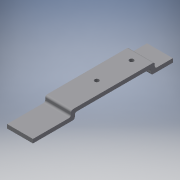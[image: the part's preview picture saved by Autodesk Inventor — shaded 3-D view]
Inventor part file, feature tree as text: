
AUTODESK INVENTOR PART (.ipt)
format: ipt  version: 2016 (Build 200138000, 138)  size: 158,208 bytes
history: native  units: mm
features: reference x9, extrude x5, sketch x5, fillet x1
ambient origin geometry x8: Origin, YZ Plane, XZ Plane, XY Plane, X Axis, Y Axis, Z Axis, Center Point
bodies: Solid1 (feature_tree)
feature tree (20):
  extrude  "Extrusion1"  Depth=130.0mm
  extrude  "Extrusion2"  Depth=6.0mm TaperAngle=0.0deg
  extrude  "Extrusion3"  Depth=6.0mm
  extrude  "Extrusion4"  Depth=34.0mm
  fillet  "Fillet1"  Radius=65.0mm
  extrude  "Extrusion5"  Depth=40.0mm
  sketch  "Sketch1"  dims[d0=40.0mm d1=130.0mm]
  sketch  "Sketch2"  dims[d2=6.0mm d3=0.0mm d4=6.0mm d5=0.0mm]
  reference  "Reference1"
  reference  "Reference2"
  sketch  "Sketch3"  dims[d6=6.0mm d7=6.0mm]
  sketch  "Sketch4"  dims[d8=3.0mm d9=0.0mm d10=34.0mm d11=65.0mm]
  sketch  "Sketch5"  dims[d12=40.0mm d13=40.0mm d14=6.0mm d15=0.0mm d16=3.0mm d17=8.0mm d18=6.0mm d19=0.0mm]
  reference  "Reference3"
  reference  "Reference4"
  reference  "Reference5"
  reference  "Reference6"
  reference  "Reference7"
  reference  "Reference8"
  reference  "Reference9"
